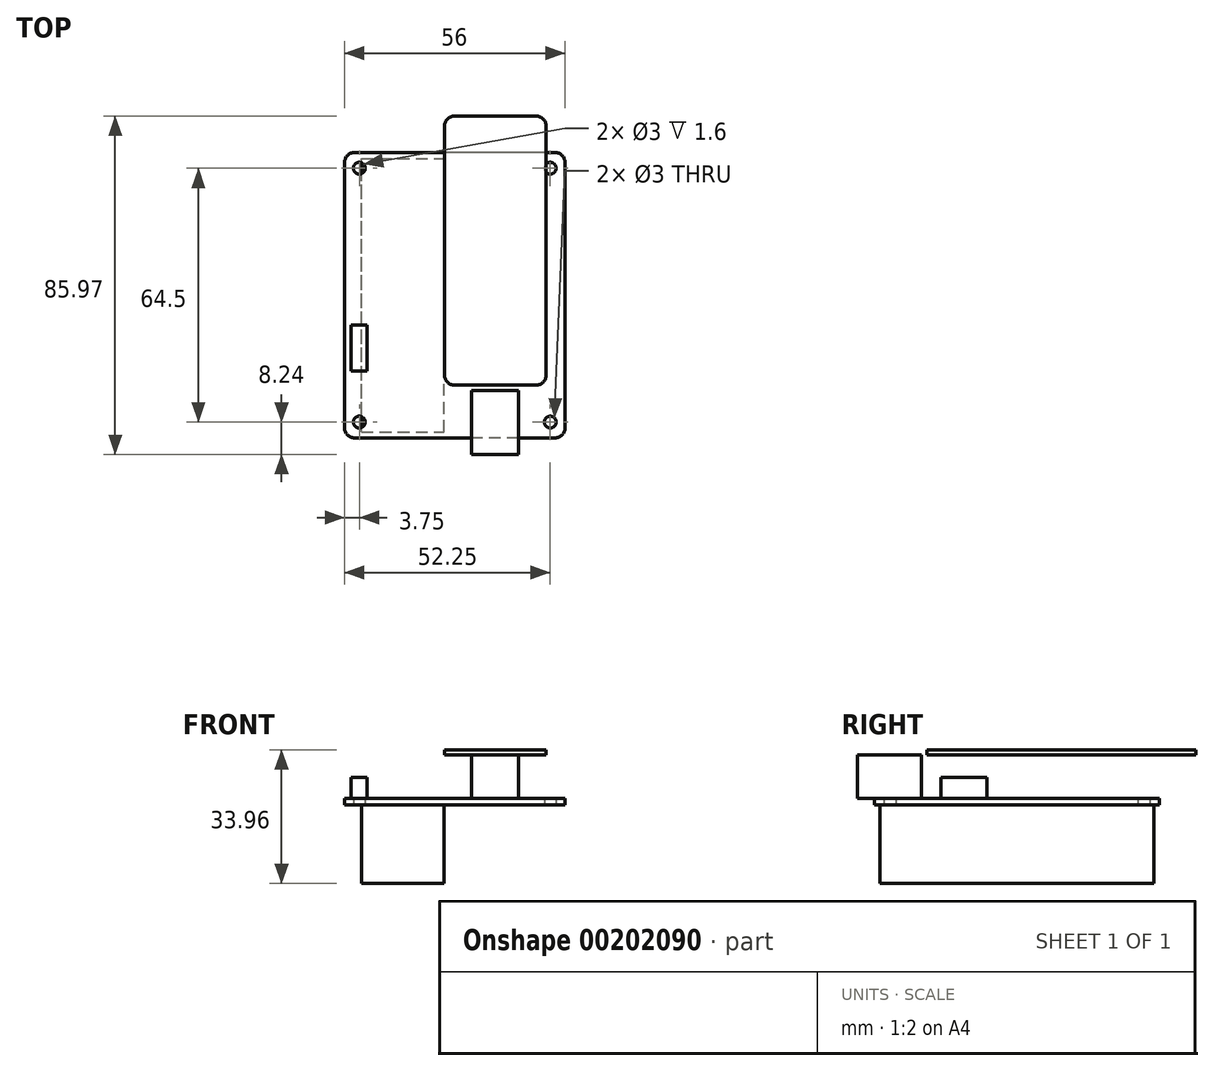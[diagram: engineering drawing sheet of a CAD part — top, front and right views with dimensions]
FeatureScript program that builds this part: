
annotation { "Feature Type Name" : "Feature", "Feature Type Description" : "" }
export const myFeature = defineFeature(function(context is Context, id is Id, definition is map)
    precondition{}
    {
        {
            var Q0;
            Q0=qCreatedBy(makeId("Top.planeOp"),FACE);
            var sketch = newSketch(context, id + "F0", { "sketchPlane" : qUnion([Q0])});
            skLineSegment(sketch, "E0.bottom", {"start": v(25.5, 36.25) * mm, "end": v(-25.5, 36.25) * mm});
            skLineSegment(sketch, "E0.top", {"start": v(25.5, -36.25) * mm, "end": v(-25.5, -36.25) * mm});
            skLineSegment(sketch, "E0.left", {"start": v(28, 33.75) * mm, "end": v(28, -33.75) * mm});
            skLineSegment(sketch, "E0.right", {"start": v(-28, 33.75) * mm, "end": v(-28, -33.75) * mm});
            skPoint(sketch, "E0.middle", {"position": v(0, 0) * mm});
            skPoint(sketch, "E1.visualSharp", {"position": v(-28, 36.25) * mm});
            skArc(sketch, "E1.filletArc", {"start": v(-25.5, 36.25) * mm, "mid": v(-27.27, 35.52) * mm, "end": v(-28, 33.75) * mm});
            skPoint(sketch, "E2.visualSharp", {"position": v(28, 36.25) * mm});
            skArc(sketch, "E2.filletArc", {"start": v(28, 33.75) * mm, "mid": v(27.27, 35.52) * mm, "end": v(25.5, 36.25) * mm});
            skPoint(sketch, "E3.visualSharp", {"position": v(28, -36.25) * mm});
            skArc(sketch, "E3.filletArc", {"start": v(25.5, -36.25) * mm, "mid": v(27.27, -35.52) * mm, "end": v(28, -33.75) * mm});
            skPoint(sketch, "E4.visualSharp", {"position": v(-28, -36.25) * mm});
            skArc(sketch, "E4.filletArc", {"start": v(-28, -33.75) * mm, "mid": v(-27.27, -35.52) * mm, "end": v(-25.5, -36.25) * mm});
            skLineSegment(sketch, "E5.bottom", {"start": v(24.25, 32.25) * mm, "end": v(-24.25, 32.25) * mm, "construction": true});
            skLineSegment(sketch, "E5.top", {"start": v(24.25, -32.25) * mm, "end": v(-24.25, -32.25) * mm, "construction": true});
            skLineSegment(sketch, "E5.left", {"start": v(24.25, 32.25) * mm, "end": v(24.25, -32.25) * mm, "construction": true});
            skLineSegment(sketch, "E5.right", {"start": v(-24.25, 32.25) * mm, "end": v(-24.25, -32.25) * mm, "construction": true});
            skCircle(sketch, "E6", {"center": v(-24.25, 32.25) * mm, "radius": 1.5 * mm});
            skCircle(sketch, "E7", {"center": v(24.25, 32.25) * mm, "radius": 1.5 * mm});
            skCircle(sketch, "E8", {"center": v(24.25, -32.25) * mm, "radius": 1.5 * mm});
            skCircle(sketch, "E9", {"center": v(-24.25, -32.25) * mm, "radius": 1.5 * mm});
            skSolve(sketch);
        }
        {
            var Q0;
            Q0 = qSketchRegion(id + "F0", true);
            extrude(context, id + "F1", {"entities" : qUnion([Q0]), "depth" : 1.6 * mm});
        }
        {
            var Q0;
            Q0=makeQuery(id+"F1.opExtrude","CAP_FACE",FACE,{"disambiguationData":[OSD([sQuery(id+"F0.wireOp",EDGE,"E0.bottom"),sQuery(id+"F0.wireOp",EDGE,"E0.top"),sQuery(id+"F0.wireOp",EDGE,"E0.left"),sQuery(id+"F0.wireOp",EDGE,"E0.right"),sQuery(id+"F0.wireOp",EDGE,"E1.filletArc"),sQuery(id+"F0.wireOp",EDGE,"E2.filletArc"),sQuery(id+"F0.wireOp",EDGE,"E3.filletArc"),sQuery(id+"F0.wireOp",EDGE,"E4.filletArc"),sQuery(id+"F0.wireOp",EDGE,"E6"),sQuery(id+"F0.wireOp",EDGE,"E7"),sQuery(id+"F0.wireOp",EDGE,"E8"),sQuery(id+"F0.wireOp",EDGE,"E9")])],"isStart":false});
            cPlane(context, id + "F2", {"entities" : qUnion([Q0]), "cplaneType" : CPlaneType.OFFSET, "offset" : 11 * mm, "width" : 150 * mm, "height" : 150 * mm});
        }
        {
            var Q0;
            Q0=qCreatedBy(id+"F2.planeOp",FACE);
            var sketch = newSketch(context, id + "F3", { "sketchPlane" : qUnion([Q0])});
            skLineSegment(sketch, "E10.bottom", {"start": v(23.2, 45.48) * mm, "end": v(-2.6, 45.48) * mm});
            skLineSegment(sketch, "E10.top", {"start": v(23.2, -22.85) * mm, "end": v(-2.6, -22.85) * mm});
            skLineSegment(sketch, "E10.left", {"start": v(23.2, 45.48) * mm, "end": v(23.2, -22.85) * mm});
            skLineSegment(sketch, "E10.right", {"start": v(-2.6, 45.48) * mm, "end": v(-2.6, -22.85) * mm});
            skPoint(sketch, "E10.middle", {"position": v(10.3, 11.32) * mm});
            skSolve(sketch);
        }
        {
            var Q0;
            Q0=makeQuery(id+"F3.imprint","IMPRINT",FACE,{"disambiguationData":[TD([[makeQuery(id+"F3.imprint","IMPRINT",EDGE,{"derivedFrom":sQuery(id+"F3.wireOp",EDGE,"E10.bottom")}),1.0]])]});
            extrude(context, id + "F4", {"entities" : qUnion([Q0]), "operationType" : NewBodyOperationType.ADD, "depth" : 1.36 * mm});
        }
        {
            var Q0;
            Q0=makeQuery(id+"F4.opExtrude","SWEPT_EDGE",EDGE,{"disambiguationData":[OSD([sQuery(id+"F3.wireOp",EDGE,"E10.top"),sQuery(id+"F3.wireOp",EDGE,"E10.left")])]});
            var Q1;
            Q1=makeQuery(id+"F4.opExtrude","SWEPT_EDGE",EDGE,{"disambiguationData":[OSD([sQuery(id+"F3.wireOp",EDGE,"E10.top"),sQuery(id+"F3.wireOp",EDGE,"E10.right")])]});
            var Q2;
            Q2=makeQuery(id+"F4.opExtrude","SWEPT_EDGE",EDGE,{"disambiguationData":[OSD([sQuery(id+"F3.wireOp",EDGE,"E10.bottom"),sQuery(id+"F3.wireOp",EDGE,"E10.left")])]});
            var Q3;
            Q3=makeQuery(id+"F4.opExtrude","SWEPT_EDGE",EDGE,{"disambiguationData":[OSD([sQuery(id+"F3.wireOp",EDGE,"E10.bottom"),sQuery(id+"F3.wireOp",EDGE,"E10.right")])]});
            fillet(context, id + "F5", {"entities" : qUnion([Q0, Q1, Q2, Q3]), "radius" : 2.5 * mm, "tangentPropagation" : true, "allowEdgeOverflow" : false});
        }
        {
            var Q0;
            Q0=makeQuery(id+"F1.opExtrude","CAP_FACE",FACE,{"disambiguationData":[OSD([sQuery(id+"F0.wireOp",EDGE,"E0.bottom"),sQuery(id+"F0.wireOp",EDGE,"E0.top"),sQuery(id+"F0.wireOp",EDGE,"E0.left"),sQuery(id+"F0.wireOp",EDGE,"E0.right"),sQuery(id+"F0.wireOp",EDGE,"E1.filletArc"),sQuery(id+"F0.wireOp",EDGE,"E2.filletArc"),sQuery(id+"F0.wireOp",EDGE,"E3.filletArc"),sQuery(id+"F0.wireOp",EDGE,"E4.filletArc"),sQuery(id+"F0.wireOp",EDGE,"E6"),sQuery(id+"F0.wireOp",EDGE,"E7"),sQuery(id+"F0.wireOp",EDGE,"E8"),sQuery(id+"F0.wireOp",EDGE,"E9")])],"isStart":false});
            var sketch = newSketch(context, id + "F6", { "sketchPlane" : qUnion([Q0])});
            skLineSegment(sketch, "E11.bottom", {"start": v(16.25, -24.22) * mm, "end": v(4.25, -24.22) * mm});
            skLineSegment(sketch, "E11.top", {"start": v(16.25, -40.5) * mm, "end": v(4.25, -40.5) * mm});
            skLineSegment(sketch, "E11.left", {"start": v(16.25, -24.22) * mm, "end": v(16.25, -40.5) * mm});
            skLineSegment(sketch, "E11.right", {"start": v(4.25, -24.22) * mm, "end": v(4.25, -40.5) * mm});
            skPoint(sketch, "E11.middle", {"position": v(10.25, -32.36) * mm});
            skSolve(sketch);
        }
        {
            var Q0;
            Q0 = qSketchRegion(id + "F6", true);
            extrude(context, id + "F7", {"entities" : qUnion([Q0]), "operationType" : NewBodyOperationType.ADD, "depth" : 11 * mm});
        }
        {
            var Q0;
            Q0=makeQuery(id+"F1.opExtrude","CAP_FACE",FACE,{"disambiguationData":[OSD([sQuery(id+"F0.wireOp",EDGE,"E0.bottom"),sQuery(id+"F0.wireOp",EDGE,"E0.top"),sQuery(id+"F0.wireOp",EDGE,"E0.left"),sQuery(id+"F0.wireOp",EDGE,"E0.right"),sQuery(id+"F0.wireOp",EDGE,"E1.filletArc"),sQuery(id+"F0.wireOp",EDGE,"E2.filletArc"),sQuery(id+"F0.wireOp",EDGE,"E3.filletArc"),sQuery(id+"F0.wireOp",EDGE,"E4.filletArc"),sQuery(id+"F0.wireOp",EDGE,"E6"),sQuery(id+"F0.wireOp",EDGE,"E7"),sQuery(id+"F0.wireOp",EDGE,"E8"),sQuery(id+"F0.wireOp",EDGE,"E9")])],"isStart":false});
            var sketch = newSketch(context, id + "F8", { "sketchPlane" : qUnion([Q0])});
            skLineSegment(sketch, "E12.bottom", {"start": v(-22.23, -7.63) * mm, "end": v(-26.33, -7.63) * mm});
            skLineSegment(sketch, "E12.top", {"start": v(-22.23, -19.25) * mm, "end": v(-26.33, -19.25) * mm});
            skLineSegment(sketch, "E12.left", {"start": v(-22.23, -7.63) * mm, "end": v(-22.23, -19.25) * mm});
            skLineSegment(sketch, "E12.right", {"start": v(-26.33, -7.63) * mm, "end": v(-26.33, -19.25) * mm});
            skPoint(sketch, "E12.middle", {"position": v(-24.28, -13.44) * mm});
            skSolve(sketch);
        }
        {
            var Q0;
            Q0 = qSketchRegion(id + "F8", true);
            extrude(context, id + "F9", {"entities" : qUnion([Q0]), "operationType" : NewBodyOperationType.ADD, "depth" : 5.3 * mm});
        }
        {
            var Q0;
            Q0=makeQuery(id+"F1.opExtrude","CAP_FACE",FACE,{"disambiguationData":[OSD([sQuery(id+"F0.wireOp",EDGE,"E0.bottom"),sQuery(id+"F0.wireOp",EDGE,"E0.top"),sQuery(id+"F0.wireOp",EDGE,"E0.left"),sQuery(id+"F0.wireOp",EDGE,"E0.right"),sQuery(id+"F0.wireOp",EDGE,"E1.filletArc"),sQuery(id+"F0.wireOp",EDGE,"E2.filletArc"),sQuery(id+"F0.wireOp",EDGE,"E3.filletArc"),sQuery(id+"F0.wireOp",EDGE,"E4.filletArc"),sQuery(id+"F0.wireOp",EDGE,"E6"),sQuery(id+"F0.wireOp",EDGE,"E7"),sQuery(id+"F0.wireOp",EDGE,"E8"),sQuery(id+"F0.wireOp",EDGE,"E9")])],"isStart":true});
            var sketch = newSketch(context, id + "F10", { "sketchPlane" : qUnion([Q0])});
            skLineSegment(sketch, "E13.bottom", {"start": v(-23.7, 34.75) * mm, "end": v(-2.7, 34.75) * mm});
            skLineSegment(sketch, "E13.top", {"start": v(-23.7, -34.75) * mm, "end": v(-2.7, -34.75) * mm});
            skLineSegment(sketch, "E13.left", {"start": v(-23.7, 34.75) * mm, "end": v(-23.7, -34.75) * mm});
            skLineSegment(sketch, "E13.right", {"start": v(-2.7, 34.75) * mm, "end": v(-2.7, -34.75) * mm});
            skPoint(sketch, "E13.middle", {"position": v(-13.2, 0) * mm});
            skLineSegment(sketch, "E14", {"start": v(0, 0) * mm, "end": v(-13.2, 0) * mm, "construction": true});
            skSolve(sketch);
        }
        {
            var Q0;
            Q0 = qSketchRegion(id + "F10", true);
            extrude(context, id + "F11", {"entities" : qUnion([Q0]), "operationType" : NewBodyOperationType.ADD, "depth" : 20 * mm});
        }
    });
